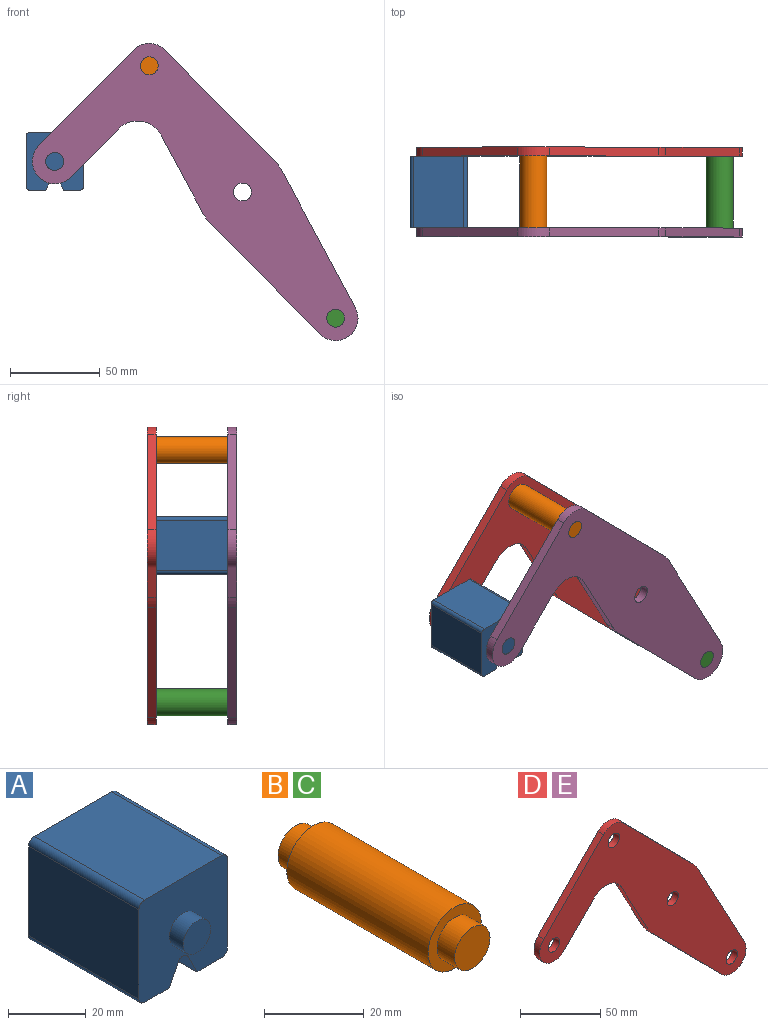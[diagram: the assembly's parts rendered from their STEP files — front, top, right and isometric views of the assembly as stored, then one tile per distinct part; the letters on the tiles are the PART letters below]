
ASSEMBLY  parts=5 mates=3
PART A: 18 faces, bbox 32.1x50x32.1 mm
  f0: plane 40x28.08mm, normal (1,0,0), area 1123.1mm2, adj f4,f10,f13,f14
  f1: plane 40x9.04mm, normal (0,0,-1), area 361.6mm2, adj f2,f4,f10,f14
  f2: plane 40x6.42mm, normal (-0.89,0,-0.45), area 287.2mm2, adj f1,f4,f10,f15
  f3: plane 40x6.42mm, normal (0.89,0,-0.45), area 287.2mm2, adj f4,f5,f10,f15
  f4: plane 32.08x32.08mm, normal (0,-1,0), area 900.6mm2, adj f0,f1,f2,f3,f5,f6,f7,f9
  f5: plane 40x9.04mm, normal (0,0,-1), area 361.6mm2, adj f3,f4,f10,f16
  f6: plane 40x28.08mm, normal (0,0,1), area 1123.1mm2, adj f4,f10,f13,f17
  f7: plane 40x28.08mm, normal (-1,0,0), area 1123.1mm2, adj f4,f10,f16,f17
  f8: plane 10x10mm, normal (0,-1,0), area 78.5mm2, adj f9
  f9: cylinder r=5mm len=10mm, axis (0,1,0), area 157.1mm2, adj f4,f8
  f10: plane 32.08x32.08mm, normal (0,1,0), area 900.6mm2, adj f0,f1,f2,f3,f5,f6,f7,f12
  f11: plane 10x10mm, normal (0,1,0), area 78.5mm2, adj f12
  f12: cylinder r=5mm len=10mm, axis (0,-1,0), area 157.1mm2, adj f10,f11
  f13: cylinder r=2mm len=40mm, axis (0,1,0), area 125.7mm2, adj f0,f4,f6,f10
  f14: cylinder r=2mm len=40mm, axis (0,-1,0), area 125.7mm2, adj f0,f1,f4,f10
  f15: cylinder r=2mm len=40mm, axis (0,1,0), area 177.1mm2, adj f2,f3,f4,f10
  f16: cylinder r=2mm len=40mm, axis (0,1,0), area 125.7mm2, adj f4,f5,f7,f10
  f17: cylinder r=2mm len=40mm, axis (0,-1,0), area 125.7mm2, adj f4,f6,f7,f10
PART B: 7 faces, bbox 15x50x15 mm
  f0: cylinder r=7.5mm len=40mm, axis (0,-1,0), area 1885mm2, adj f2,f5
  f1: cylinder r=5mm len=10mm, axis (0,1,0), area 157.1mm2, adj f2,f3
  f2: plane 15x15mm, normal (0,-1,0), area 98.2mm2, adj f0,f1
  f3: plane 10x10mm, normal (0,-1,0), area 78.5mm2, adj f1
  f4: cylinder r=5mm len=10mm, axis (0,-1,0), area 157.1mm2, adj f5,f6
  f5: plane 15x15mm, normal (0,1,0), area 98.2mm2, adj f0,f4
  f6: plane 10x10mm, normal (0,1,0), area 78.5mm2, adj f4
PART C: same geometry as B
PART D: 18 faces, bbox 181.7x5x165.8 mm
  f0: plane 43.49x23.35mm, normal (-0.88,0,-0.47), area 246.8mm2, adj f1,f14,f16,f17
  f1: cylinder r=25mm len=5.75mm, axis (0,1,0), area 35.8mm2, adj f0,f2,f16,f17
  f2: plane 61.6x60.87mm, normal (-0.71,0,-0.7), area 433mm2, adj f1,f3,f16,f17
  f3: cylinder r=12.5mm len=21.39mm, axis (0,1,0), area 178.4mm2, adj f2,f4,f16,f17
  f4: plane 76.3x40.96mm, normal (0.88,0,0.47), area 433mm2, adj f3,f5,f16,f17
  f5: cylinder r=25mm len=5.75mm, axis (0,1,0), area 35.8mm2, adj f4,f6,f16,f17
  f6: plane 61.6x60.87mm, normal (0.71,0,0.7), area 433mm2, adj f5,f7,f16,f17
  f7: cylinder r=12.5mm len=17.78mm, axis (0,1,0), area 98.9mm2, adj f6,f8,f16,f17
  f8: plane 53.35x52.71mm, normal (-0.71,0,0.7), area 375mm2, adj f7,f9,f16,f17
  f9: cylinder r=12.5mm len=21.39mm, axis (0,1,0), area 196.3mm2, adj f8,f10,f16,f17
  f10: plane 26.86x26.54mm, normal (0.71,0,-0.7), area 188.8mm2, adj f9,f14,f16,f17
  f11: cylinder r=5mm len=10mm, axis (0,1,0), area 157.1mm2, adj f16,f17
  f12: cylinder r=5mm len=10mm, axis (0,1,0), area 157.1mm2, adj f16,f17
  f13: cylinder r=5mm len=10mm, axis (0,1,0), area 157.1mm2, adj f16,f17
  f14: cylinder r=15mm len=23.89mm, axis (0,1,0), area 140.2mm2, adj f0,f10,f16,f17
  f15: cylinder r=5mm len=10mm, axis (0,1,0), area 157.1mm2, adj f16,f17
  f16: plane 181.66x165.78mm, normal (0,-1,0), area 8710.1mm2, adj f0,f1,f2,f3,f4,f5,f6,f7
  f17: plane 181.66x165.78mm, normal (0,1,0), area 8710.1mm2, adj f0,f1,f2,f3,f4,f5,f6,f7
PART E: same geometry as D
PLACE A t=(0,-20,0)mm
PLACE B t=(0,-20,0)mm
PLACE C t=(103.95,-20,-140.78)mm
PLACE D t=(0,25,0)mm
PLACE E t=(0,-20,0)mm fixed
MATE fastened D.f7 <-> B.f0  axis (0,-1,0) through (-51.98,20,70.39)mm
MATE fastened C.f0 <-> E.f3  axis (0,-1,0) through (51.98,-20,-70.39)mm
MATE revolute A.f9 <-> E.f9  axis (0,-1,0) through (-104.69,-20,17.04)mm
